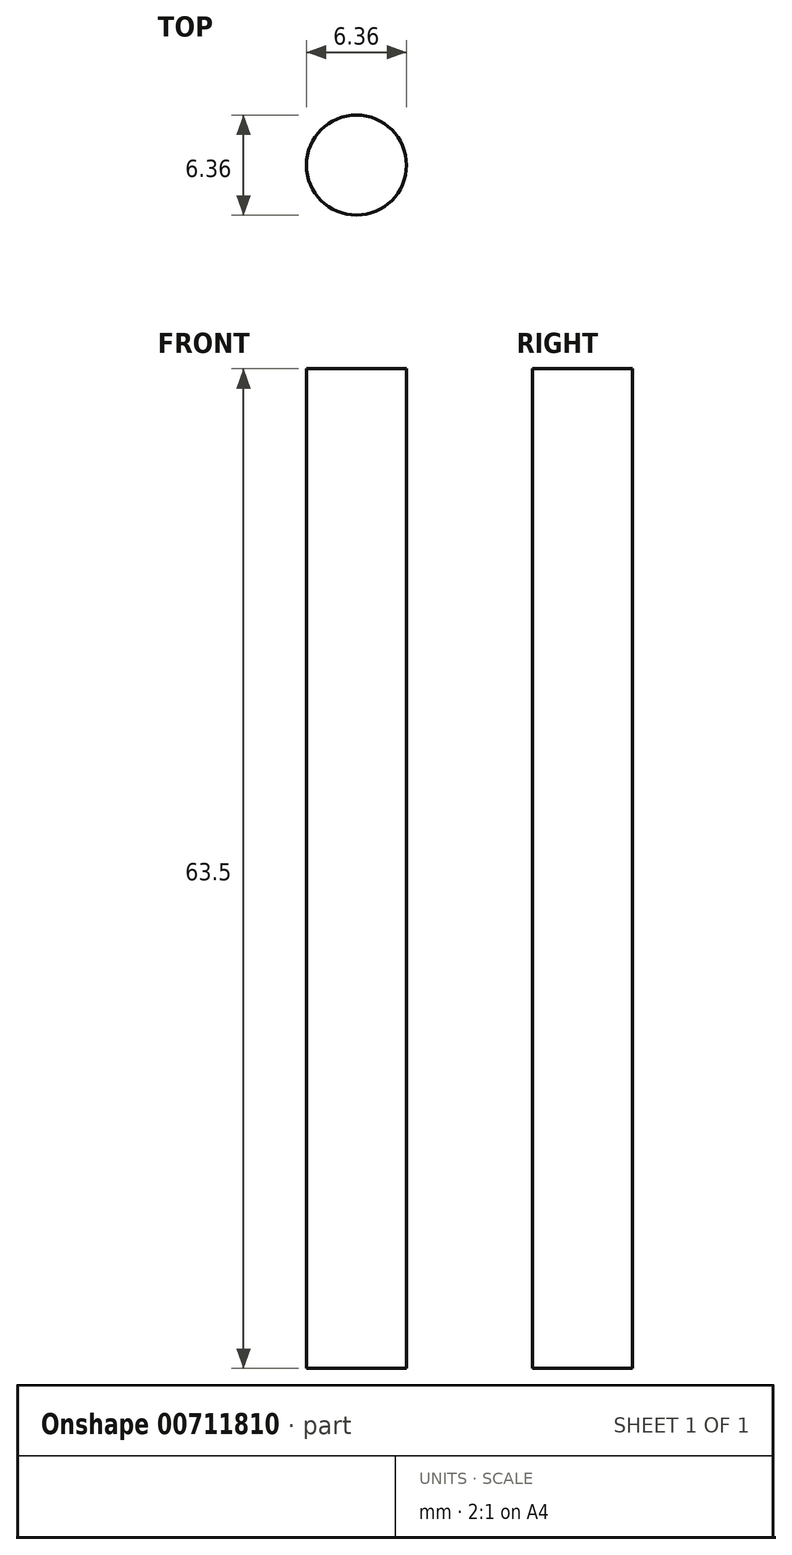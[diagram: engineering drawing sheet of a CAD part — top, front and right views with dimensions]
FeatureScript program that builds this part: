
annotation { "Feature Type Name" : "Feature", "Feature Type Description" : "" }
export const myFeature = defineFeature(function(context is Context, id is Id, definition is map)
    precondition{}
    {
        {
            var Q0;
            Q0=qCreatedBy(makeId("Top.planeOp"),FACE);
            var sketch = newSketch(context, id + "F0", { "sketchPlane" : qUnion([Q0])});
            skCircle(sketch, "E0", {"center": v(0, 0) * mm, "radius": 3.18 * mm});
            skSolve(sketch);
        }
        {
            var Q0;
            Q0 = qSketchRegion(id + "F0", true);
            extrude(context, id + "F1", {"entities" : qUnion([Q0]), "depth" : 63.5 * mm, "offsetDistance" : 25.4 * mm});
        }
    });
